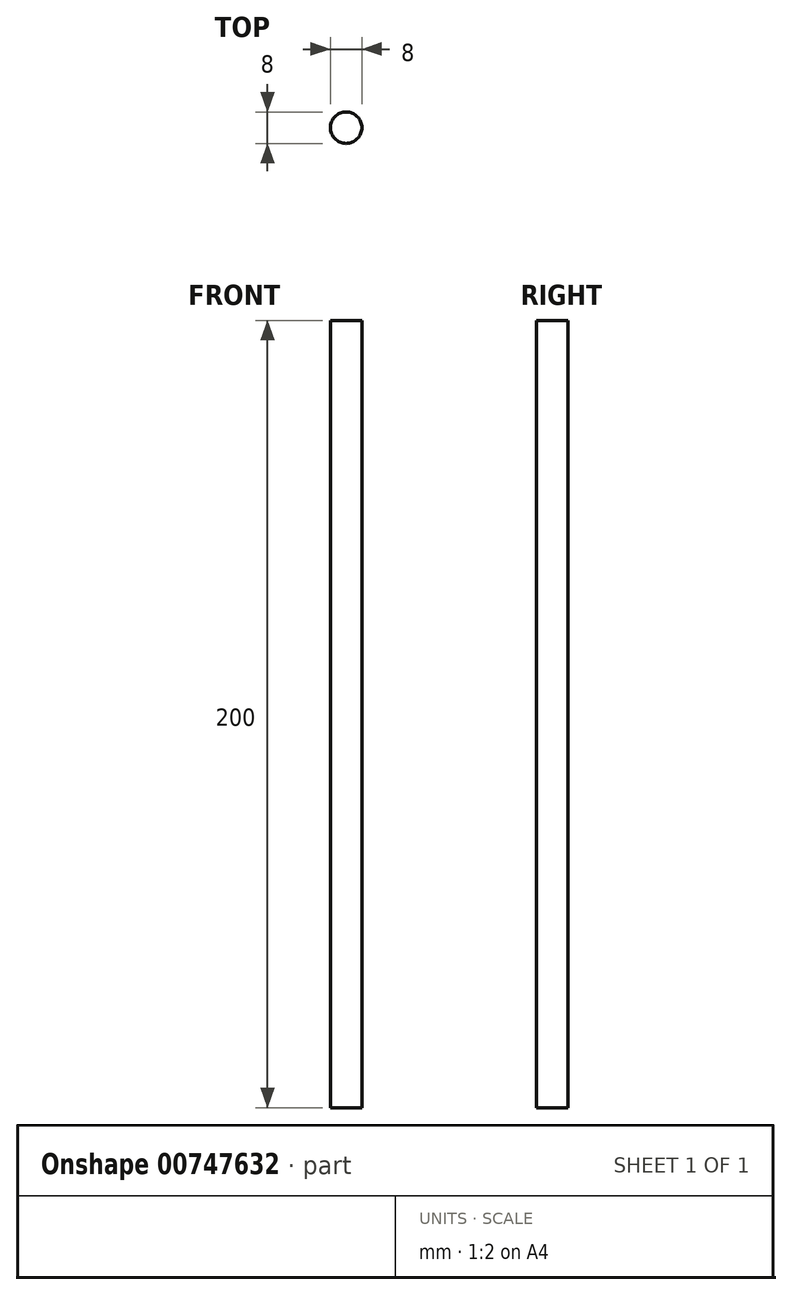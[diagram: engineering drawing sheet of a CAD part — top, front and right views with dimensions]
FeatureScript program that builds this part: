
annotation { "Feature Type Name" : "Feature", "Feature Type Description" : "" }
export const myFeature = defineFeature(function(context is Context, id is Id, definition is map)
    precondition{}
    {
        {
            var Q0;
            Q0=qCreatedBy(makeId("Top.planeOp"),FACE);
            var sketch = newSketch(context, id + "F0", { "sketchPlane" : qUnion([Q0])});
            skCircle(sketch, "E0", {"center": v(0, 0) * mm, "radius": 4 * mm});
            skSolve(sketch);
        }
        {
            var Q0;
            Q0 = qSketchRegion(id + "F0", true);
            extrude(context, id + "F1", {"entities" : qUnion([Q0]), "depth" : 200 * mm, "offsetDistance" : 25.4 * mm});
        }
    });
